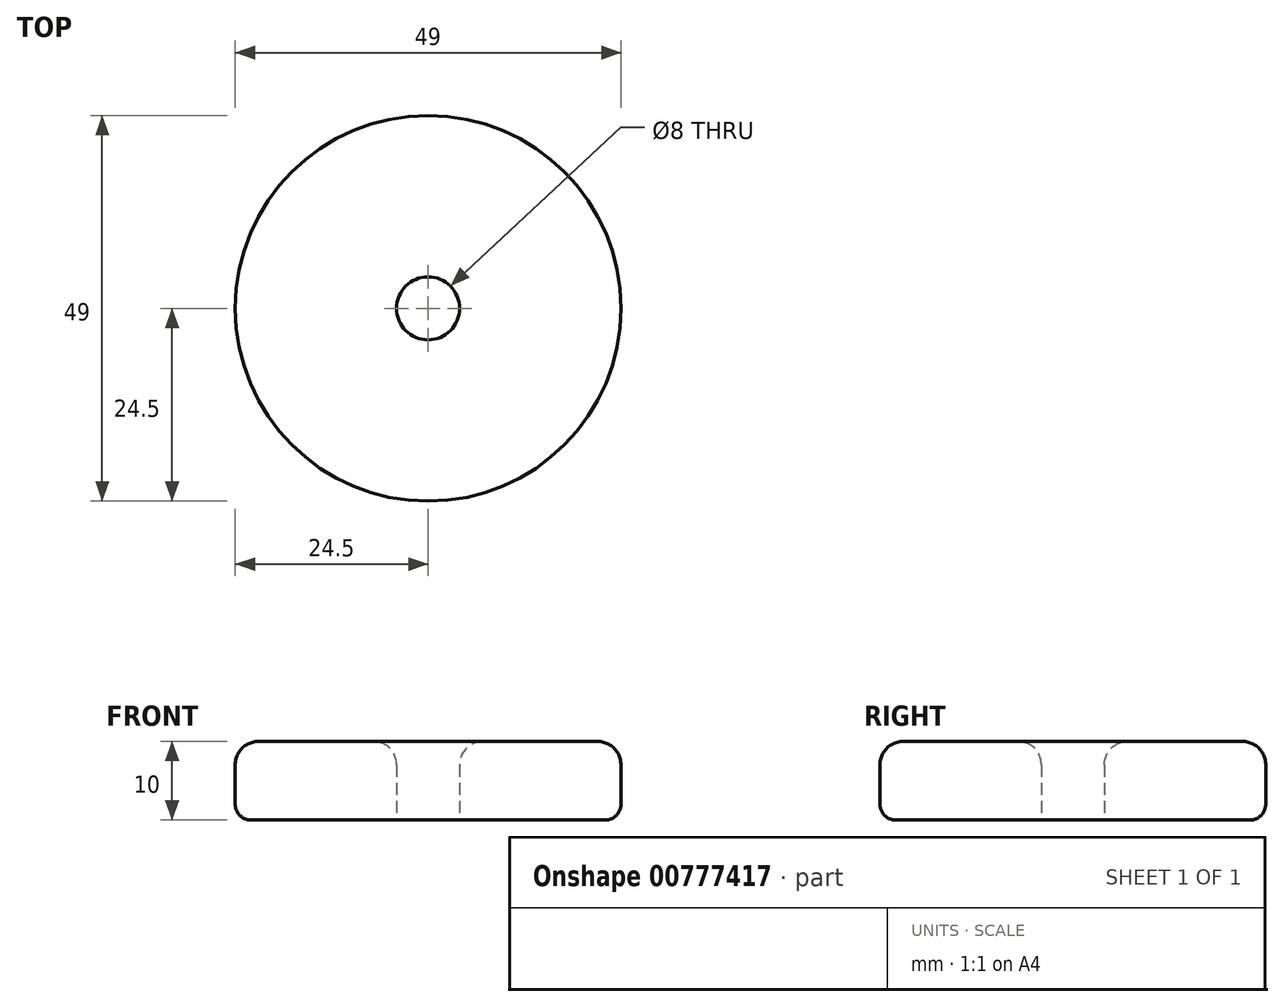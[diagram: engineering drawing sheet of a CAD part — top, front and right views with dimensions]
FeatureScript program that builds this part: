
annotation { "Feature Type Name" : "Feature", "Feature Type Description" : "" }
export const myFeature = defineFeature(function(context is Context, id is Id, definition is map)
    precondition{}
    {
        {
            var Q0;
            Q0=qCreatedBy(makeId("Top.planeOp"),FACE);
            var sketch = newSketch(context, id + "F0", { "sketchPlane" : qUnion([Q0])});
            skCircle(sketch, "E0", {"center": v(0, 0) * mm, "radius": 24.5 * mm});
            skCircle(sketch, "E1", {"center": v(0, 0) * mm, "radius": 4 * mm});
            skCircle(sketch, "E2", {"center": v(0, 0) * mm, "radius": 32.24 * mm});
            skSolve(sketch);
        }
        {
            var Q0;
            Q0=makeQuery(id+"F0.imprint","IMPRINT",FACE,{"disambiguationData":[TD([[makeQuery(id+"F0.imprint","IMPRINT",EDGE,{"derivedFrom":sQuery(id+"F0.wireOp",EDGE,"E0")}),1.0]])]});
            extrude(context, id + "F1", {"entities" : qUnion([Q0]), "depth" : 10 * mm, "offsetDistance" : 25 * mm});
        }
        {
            var Q0;
            Q0=makeQuery(id+"F1.opExtrude","CAP_FACE",FACE,{"disambiguationData":[OSD([sQuery(id+"F0.wireOp",EDGE,"E0"),sQuery(id+"F0.wireOp",EDGE,"E1")])],"isStart":false});
            var Q1;
            Q1=makeQuery(id+"F1.opExtrude","CAP_EDGE",EDGE,{"disambiguationData":[OSD([sQuery(id+"F0.wireOp",EDGE,"E1")])],"isStart":false});
            fillet(context, id + "F2", {"entities" : qUnion([Q0, Q1]), "radius" : 3 * mm, "tangentPropagation" : true, "allowEdgeOverflow" : false});
        }
        {
            var Q0;
            Q0=makeQuery(id+"F1.opExtrude","CAP_EDGE",EDGE,{"disambiguationData":[OSD([sQuery(id+"F0.wireOp",EDGE,"E0")])],"isStart":true});
            fillet(context, id + "F3", {"entities" : qUnion([Q0]), "radius" : 2 * mm, "tangentPropagation" : true, "allowEdgeOverflow" : false});
        }
    });
